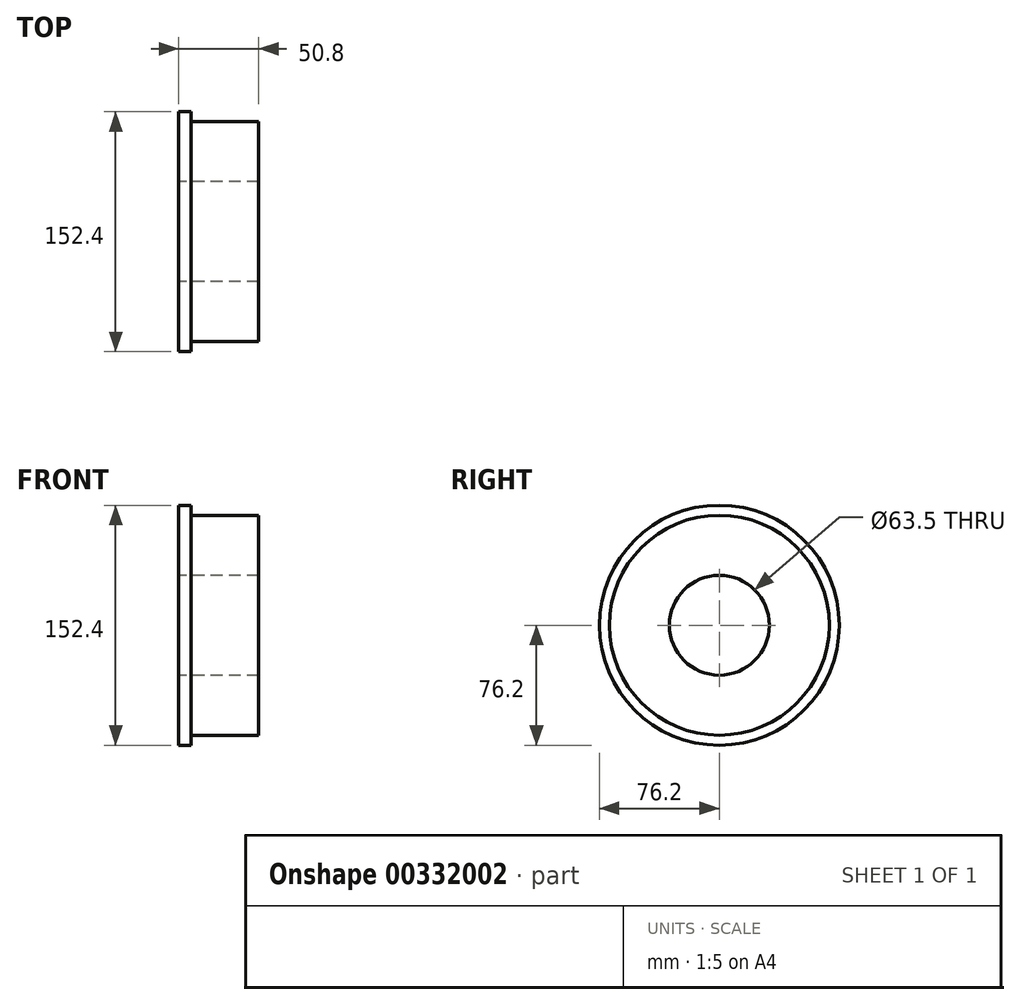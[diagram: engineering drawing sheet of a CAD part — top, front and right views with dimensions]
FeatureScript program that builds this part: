
annotation { "Feature Type Name" : "Feature", "Feature Type Description" : "" }
export const myFeature = defineFeature(function(context is Context, id is Id, definition is map)
    precondition{}
    {
        {
            var Q0;
            Q0=qCreatedBy(makeId("Right.planeOp"),FACE);
            var sketch = newSketch(context, id + "F0", { "sketchPlane" : qUnion([Q0])});
            skCircle(sketch, "E0", {"center": v(0, 0) * mm, "radius": 69.85 * mm});
            skCircle(sketch, "E1", {"center": v(0, 0) * mm, "radius": 31.75 * mm});
            skSolve(sketch);
        }
        {
            var Q0;
            Q0 = qSketchRegion(id + "F0", true);
            extrude(context, id + "F1", {"entities" : qUnion([Q0]), "depth" : 42.93 * mm});
        }
        {
            var Q0;
            Q0=makeQuery(id+"F1.opExtrude","CAP_FACE",FACE,{"disambiguationData":[OSD([sQuery(id+"F0.wireOp",EDGE,"E0"),sQuery(id+"F0.wireOp",EDGE,"E1")])],"isStart":true});
            var sketch = newSketch(context, id + "F2", { "sketchPlane" : qUnion([Q0])});
            skCircle(sketch, "E2", {"center": v(0, 0) * mm, "radius": 76.2 * mm});
            skCircle(sketch, "E3.0", {"center": v(0, 0) * mm, "radius": 31.75 * mm});
            skSolve(sketch);
        }
        {
            var Q0;
            Q0 = qSketchRegion(id + "F2", true);
            extrude(context, id + "F3", {"entities" : qUnion([Q0]), "operationType" : NewBodyOperationType.ADD, "depth" : 7.87 * mm});
        }
    });
